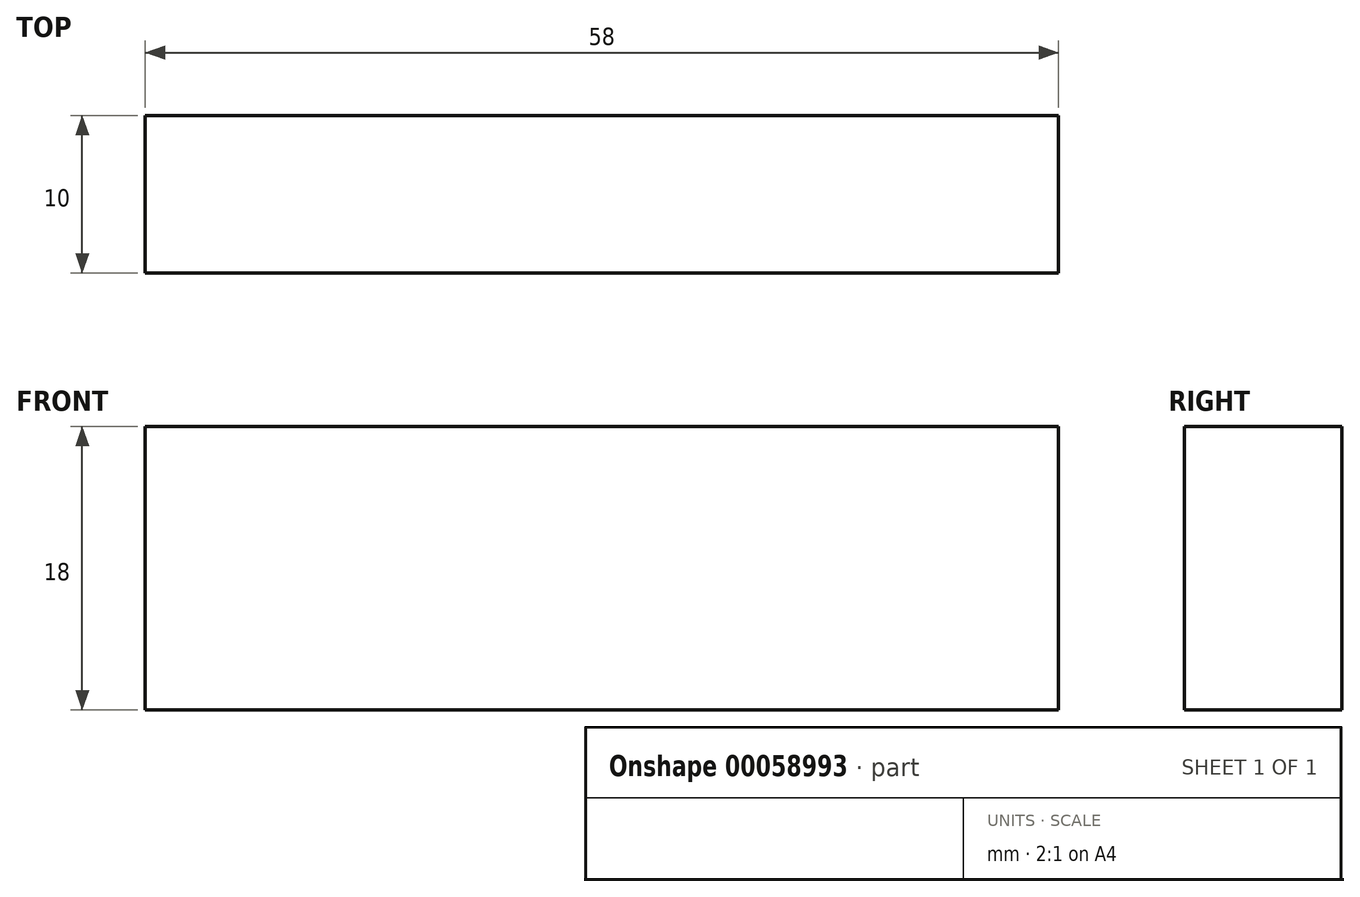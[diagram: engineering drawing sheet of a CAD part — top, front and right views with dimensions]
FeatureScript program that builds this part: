
annotation { "Feature Type Name" : "Feature", "Feature Type Description" : "" }
export const myFeature = defineFeature(function(context is Context, id is Id, definition is map)
    precondition{}
    {
        {
            var Q0;
            Q0=qCreatedBy(makeId("Front.planeOp"),FACE);
            var sketch = newSketch(context, id + "F0", { "sketchPlane" : qUnion([Q0])});
            skLineSegment(sketch, "E0.bottom", {"start": v(-15.18, 14.83) * mm, "end": v(42.82, 14.83) * mm});
            skLineSegment(sketch, "E0.top", {"start": v(-15.18, -3.17) * mm, "end": v(42.82, -3.17) * mm});
            skLineSegment(sketch, "E0.left", {"start": v(-15.18, 14.83) * mm, "end": v(-15.18, -3.17) * mm});
            skLineSegment(sketch, "E0.right", {"start": v(42.82, 14.83) * mm, "end": v(42.82, -3.17) * mm});
            skSolve(sketch);
        }
        {
            var Q0;
            Q0 = qSketchRegion(id + "F0", true);
            extrude(context, id + "F1", {"entities" : qUnion([Q0]), "depth" : 10 * mm});
        }
    });
